# Revit family: Plumbing_Fixtures_Grohe_Eurocube_Shower_Mixer_Lever_19898000_14_METRIC
name_source: partatom
category: Plumbing Fixtures
revit_build: Autodesk Revit 2014 (Build: 20130308_1515(x64)
units: mm (PartAtom-declared; Revit-internal decimal feet)

## types (1)
- Plumbing_Fixtures_Grohe_Eurocube_Shower_Mixer_Lever_19898000_14_METRIC
    ADA Compliant = Yes
    Assembly Code = C1030220
    AssetType = Fixed
    CW Connection = Yes
    CWFU = 4.5
    ClassificationName = Uniclass2015
    ClassificationValue = Pr_40_20_87_78
    Cold Water Conection Diamiter = 10 mm  [stored 0.0328084 ft]
    Cold Water Radius = 5 mm  [stored 0.0164042 ft]
    Color = Chrome
    Cost = 0 $
    Default Elevation = 600 mm
    Description = Single-lever shower mixer (Chrome)
    DocumentationCertificates = http://www.grohe.com
    DocumentationInstallationGuide = http://www.grohe.com
    DocumentationLiterature = http://cdn08.grohe.com
    DocumentationMaintenance = http://projects.grohe.com
    DocumentationTechnical = http://cdn08.grohe.com
    DurationUnit = Years
    Ecojoy = No
    ExpectedLife = 0
    Finish = Chrome
    Flow Rate = 20L/min (Spout) 7L/min (Shower)
    HW Connection = Yes
    HWFU = 4.5
    Height = 482 mm  [stored 1.58136 ft]
    Hot Water Conection Diamiter = 10 mm  [stored 0.0328084 ft]
    Hot Water Radius = 5 mm  [stored 0.0164042 ft]
    Keynote = N13
    Length = 184 mm  [stored 0.603675 ft]
    Low Emitting Material = Yes
    Manufacturer = Grohe AG
    Material = Chrome
    Mixing Leaver = Yes
    Model = Eurocube Shower Mixer - 19898000
    ModelNumber = Eurocube Shower Mixer - 19898000
    NBSDescription = Shower manual water supply sets
    NBSObjectName = Shower mixers
    NBSReference = 45-35-70/335
    Name = Eurocube Shower Mixer - 19898000
    No of Holes = 1
    Operating Pressure = 10 bar
    Percentage of Recycled Content = 0
    Product Documentation Link = http://cdn08.grohe.com
    Product Page URL = http://www.grohe.com
    ProductionYear = 2015
    Pull out or Pull Down = Pull Out
    TagNumber = Single-lever shower mixer (Chrome)
    Type Comments = Single-lever shower mixer (Chrome)
    URL = www.grohe.com
    Valve Spacing = 34 mm
    Vent Connection = No
    WFU = 0
    WarrantyDurationUnit = Years
    Waste Connection = No
    Width = 95 mm
    _BIMspec_GUID = 0
    _current revision = 2
    _distributed by = www.bimstore.co.uk

note: [stored X ft] marks values corroborated as IEEE doubles in the binary element streams (Revit-internal decimal feet)

## geometry (parser evidence)
native form markers: Blend x6, Sweep x1
no freeform markers — native parametric forms only
